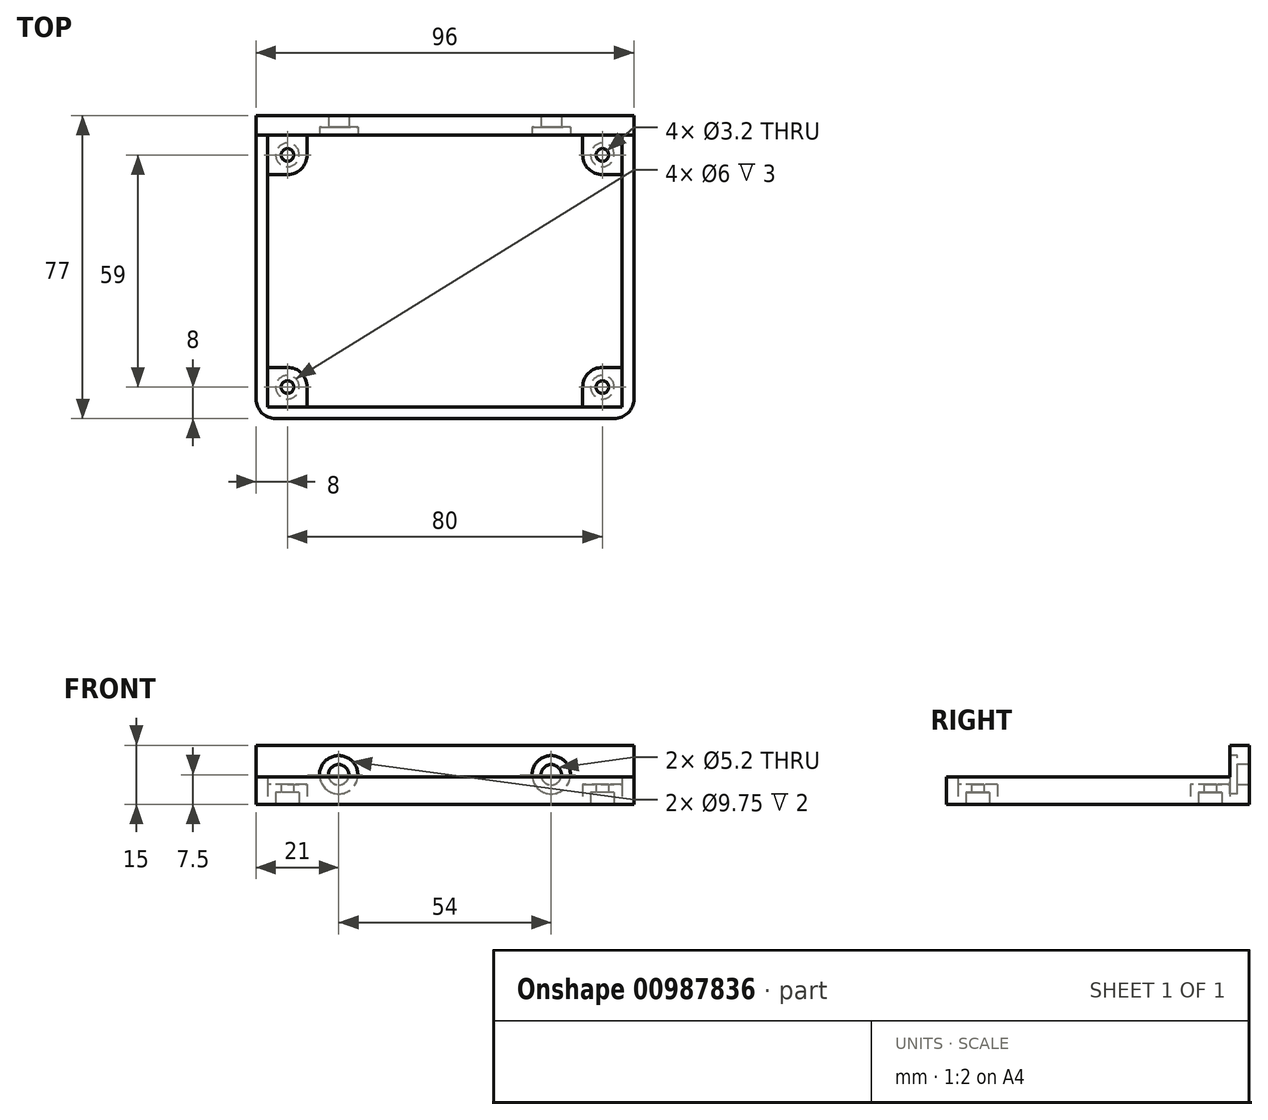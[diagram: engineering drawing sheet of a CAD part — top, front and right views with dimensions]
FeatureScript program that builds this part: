
annotation { "Feature Type Name" : "Feature", "Feature Type Description" : "" }
export const myFeature = defineFeature(function(context is Context, id is Id, definition is map)
    precondition{}
    {
        {
            var Q0;
            Q0=qCreatedBy(makeId("Top.planeOp"),FACE);
            var sketch = newSketch(context, id + "F0", { "sketchPlane" : qUnion([Q0])});
            skLineSegment(sketch, "E0.bottom", {"start": v(-40, 29.5) * mm, "end": v(40, 29.5) * mm, "construction": true});
            skLineSegment(sketch, "E0.top", {"start": v(-40, -29.5) * mm, "end": v(40, -29.5) * mm, "construction": true});
            skLineSegment(sketch, "E0.left", {"start": v(-40, 29.5) * mm, "end": v(-40, -29.5) * mm, "construction": true});
            skLineSegment(sketch, "E0.right", {"start": v(40, 29.5) * mm, "end": v(40, -29.5) * mm, "construction": true});
            skPoint(sketch, "E0.middle", {"position": v(0, 0) * mm});
            skLineSegment(sketch, "E1.bottom", {"start": v(-45, 34.5) * mm, "end": v(45, 34.5) * mm});
            skLineSegment(sketch, "E1.top", {"start": v(-45, -34.5) * mm, "end": v(45, -34.5) * mm});
            skLineSegment(sketch, "E1.left", {"start": v(-45, 34.5) * mm, "end": v(-45, -34.5) * mm});
            skLineSegment(sketch, "E1.right", {"start": v(45, 34.5) * mm, "end": v(45, -34.5) * mm});
            skCircle(sketch, "E2", {"center": v(-40, 29.5) * mm, "radius": 1.6 * mm});
            skCircle(sketch, "E3", {"center": v(-40, -29.5) * mm, "radius": 1.6 * mm});
            skCircle(sketch, "E4", {"center": v(40, -29.5) * mm, "radius": 1.6 * mm});
            skCircle(sketch, "E5", {"center": v(40, 29.5) * mm, "radius": 1.6 * mm});
            skCircle(sketch, "E6", {"center": v(-40, -29.5) * mm, "radius": 5 * mm});
            skLineSegment(sketch, "E7", {"start": v(-35, -29.5) * mm, "end": v(-35, -34.5) * mm});
            skLineSegment(sketch, "E8", {"start": v(-40, -24.5) * mm, "end": v(-45, -24.5) * mm});
            skCircle(sketch, "E9", {"center": v(-40, 29.5) * mm, "radius": 5 * mm});
            skCircle(sketch, "E10", {"center": v(40, 29.5) * mm, "radius": 5 * mm});
            skLineSegment(sketch, "E11", {"start": v(40, 24.5) * mm, "end": v(45, 24.5) * mm});
            skCircle(sketch, "E12", {"center": v(40, -29.5) * mm, "radius": 5 * mm});
            skLineSegment(sketch, "E13", {"start": v(35, -29.5) * mm, "end": v(35, -34.5) * mm});
            skLineSegment(sketch, "E14", {"start": v(40, -24.5) * mm, "end": v(45, -24.5) * mm});
            skLineSegment(sketch, "E15", {"start": v(35, 29.5) * mm, "end": v(35, 34.5) * mm});
            skLineSegment(sketch, "E16.bottom", {"start": v(-48, 39.5) * mm, "end": v(48, 39.5) * mm});
            skLineSegment(sketch, "E16.top", {"start": v(-48, -37.5) * mm, "end": v(48, -37.5) * mm});
            skLineSegment(sketch, "E16.left", {"start": v(-48, 39.5) * mm, "end": v(-48, -37.5) * mm});
            skLineSegment(sketch, "E16.right", {"start": v(48, 39.5) * mm, "end": v(48, -37.5) * mm});
            skLineSegment(sketch, "E17", {"start": v(-35, 29.5) * mm, "end": v(-35, 34.5) * mm});
            skLineSegment(sketch, "E18", {"start": v(-40, 24.5) * mm, "end": v(-45, 24.5) * mm});
            skCircle(sketch, "E19", {"center": v(40, 29.5) * mm, "radius": 3 * mm});
            skCircle(sketch, "E20", {"center": v(-40, 29.5) * mm, "radius": 3 * mm});
            skCircle(sketch, "E21", {"center": v(-40, -29.5) * mm, "radius": 3 * mm});
            skCircle(sketch, "E22", {"center": v(40, -29.5) * mm, "radius": 3 * mm});
            skLineSegment(sketch, "E23.top", {"start": v(-48, 34.5) * mm, "end": v(48, 34.5) * mm});
            skLineSegment(sketch, "E23.left", {"start": v(-48, 39.5) * mm, "end": v(-48, 34.5) * mm});
            skLineSegment(sketch, "E23.right", {"start": v(48, 39.5) * mm, "end": v(48, 34.5) * mm});
            skSolve(sketch);
        }
        {
            var Q0;
            Q0=makeQuery(id+"F0.imprint","IMPRINT",FACE,{"disambiguationData":[TD([[makeQuery(id+"F0.imprint","IMPRINT",EDGE,{"derivedFrom":sQuery(id+"F0.wireOp",EDGE,"E16.bottom")}),-1.0]])]});
            var Q1;
            {var subQ0=sQuery(id+"F0.wireOp",EDGE,"E7");Q1=makeQuery(id+"F0.imprint","IMPRINT",FACE,{"disambiguationData":[TD([[makeQuery(id+"F0.imprint","IMPRINT",EDGE,{"derivedFrom":subQ0}),-1.0]])]});}
            var Q2;
            {var subQ0=sQuery(id+"F0.wireOp",EDGE,"E1.left");var subQ1=sQuery(id+"F0.wireOp",EDGE,"E1.top");var subQ2=makeQuery(id+"F0.imprint","INTERSECT",VERTEX,{"derivedFrom":[subQ1,subQ0]});Q2=makeQuery(id+"F0.imprint","IMPRINT",FACE,{"disambiguationData":[TD([[makeQuery(id+"F0.imprint","IMPRINT",EDGE,{"disambiguationData":[TD([[subQ2,-1.0]])],"derivedFrom":subQ1}),1.0]])]});}
            var Q3;
            {var subQ0=sQuery(id+"F0.wireOp",EDGE,"E8");Q3=makeQuery(id+"F0.imprint","IMPRINT",FACE,{"disambiguationData":[TD([[makeQuery(id+"F0.imprint","IMPRINT",EDGE,{"derivedFrom":subQ0}),1.0]])]});}
            var Q4;
            Q4=makeQuery(id+"F0.imprint","IMPRINT",FACE,{"disambiguationData":[TD([[makeQuery(id+"F0.imprint","IMPRINT",EDGE,{"derivedFrom":sQuery(id+"F0.wireOp",EDGE,"E3")}),-1.0]])]});
            var Q5;
            {var subQ0=sQuery(id+"F0.wireOp",EDGE,"E13");Q5=makeQuery(id+"F0.imprint","IMPRINT",FACE,{"disambiguationData":[TD([[makeQuery(id+"F0.imprint","IMPRINT",EDGE,{"derivedFrom":subQ0}),1.0]])]});}
            var Q6;
            {var subQ0=sQuery(id+"F0.wireOp",EDGE,"E14");Q6=makeQuery(id+"F0.imprint","IMPRINT",FACE,{"disambiguationData":[TD([[makeQuery(id+"F0.imprint","IMPRINT",EDGE,{"derivedFrom":subQ0}),-1.0]])]});}
            var Q7;
            {var subQ0=sQuery(id+"F0.wireOp",EDGE,"E1.right");var subQ1=sQuery(id+"F0.wireOp",EDGE,"E1.top");var subQ2=makeQuery(id+"F0.imprint","INTERSECT",VERTEX,{"derivedFrom":[subQ1,subQ0]});Q7=makeQuery(id+"F0.imprint","IMPRINT",FACE,{"disambiguationData":[TD([[makeQuery(id+"F0.imprint","IMPRINT",EDGE,{"disambiguationData":[TD([[subQ2,1.0]])],"derivedFrom":subQ1}),1.0]])]});}
            var Q8;
            Q8=makeQuery(id+"F0.imprint","IMPRINT",FACE,{"disambiguationData":[TD([[makeQuery(id+"F0.imprint","IMPRINT",EDGE,{"derivedFrom":sQuery(id+"F0.wireOp",EDGE,"E4")}),-1.0]])]});
            var Q9;
            {var subQ0=sQuery(id+"F0.wireOp",EDGE,"E11");Q9=makeQuery(id+"F0.imprint","IMPRINT",FACE,{"disambiguationData":[TD([[makeQuery(id+"F0.imprint","IMPRINT",EDGE,{"derivedFrom":subQ0}),1.0]])]});}
            var Q10;
            {var subQ0=sQuery(id+"F0.wireOp",EDGE,"E1.right");var subQ1=sQuery(id+"F0.wireOp",EDGE,"E1.bottom");var subQ2=makeQuery(id+"F0.imprint","INTERSECT",VERTEX,{"derivedFrom":[subQ1,subQ0]});Q10=makeQuery(id+"F0.imprint","IMPRINT",FACE,{"disambiguationData":[TD([[makeQuery(id+"F0.imprint","IMPRINT",EDGE,{"disambiguationData":[TD([[subQ2,1.0]])],"derivedFrom":subQ1}),-1.0]])]});}
            var Q11;
            {var subQ0=sQuery(id+"F0.wireOp",EDGE,"E15");Q11=makeQuery(id+"F0.imprint","IMPRINT",FACE,{"disambiguationData":[TD([[makeQuery(id+"F0.imprint","IMPRINT",EDGE,{"derivedFrom":subQ0}),-1.0]])]});}
            var Q12;
            Q12=makeQuery(id+"F0.imprint","IMPRINT",FACE,{"disambiguationData":[TD([[makeQuery(id+"F0.imprint","IMPRINT",EDGE,{"derivedFrom":sQuery(id+"F0.wireOp",EDGE,"E5")}),-1.0]])]});
            var Q13;
            {var subQ0=sQuery(id+"F0.wireOp",EDGE,"E17");Q13=makeQuery(id+"F0.imprint","IMPRINT",FACE,{"disambiguationData":[TD([[makeQuery(id+"F0.imprint","IMPRINT",EDGE,{"derivedFrom":subQ0}),1.0]])]});}
            var Q14;
            {var subQ0=sQuery(id+"F0.wireOp",EDGE,"E1.left");var subQ1=sQuery(id+"F0.wireOp",EDGE,"E1.bottom");var subQ2=makeQuery(id+"F0.imprint","INTERSECT",VERTEX,{"derivedFrom":[subQ1,subQ0]});Q14=makeQuery(id+"F0.imprint","IMPRINT",FACE,{"disambiguationData":[TD([[makeQuery(id+"F0.imprint","IMPRINT",EDGE,{"disambiguationData":[TD([[subQ2,-1.0]])],"derivedFrom":subQ1}),-1.0]])]});}
            var Q15;
            {var subQ0=sQuery(id+"F0.wireOp",EDGE,"E18");Q15=makeQuery(id+"F0.imprint","IMPRINT",FACE,{"disambiguationData":[TD([[makeQuery(id+"F0.imprint","IMPRINT",EDGE,{"derivedFrom":subQ0}),-1.0]])]});}
            var Q16;
            Q16=makeQuery(id+"F0.imprint","IMPRINT",FACE,{"disambiguationData":[TD([[makeQuery(id+"F0.imprint","IMPRINT",EDGE,{"derivedFrom":sQuery(id+"F0.wireOp",EDGE,"E2")}),-1.0]])]});
            var Q17;
            Q17=makeQuery(id+"F0.imprint","IMPRINT",FACE,{"disambiguationData":[TD([[makeQuery(id+"F0.imprint","IMPRINT",EDGE,{"derivedFrom":sQuery(id+"F0.wireOp",EDGE,"E22")}),-1.0]])]});
            var Q18;
            Q18=makeQuery(id+"F0.imprint","IMPRINT",FACE,{"disambiguationData":[TD([[makeQuery(id+"F0.imprint","IMPRINT",EDGE,{"derivedFrom":sQuery(id+"F0.wireOp",EDGE,"E21")}),-1.0]])]});
            var Q19;
            Q19=makeQuery(id+"F0.imprint","IMPRINT",FACE,{"disambiguationData":[TD([[makeQuery(id+"F0.imprint","IMPRINT",EDGE,{"derivedFrom":sQuery(id+"F0.wireOp",EDGE,"E20")}),-1.0]])]});
            var Q20;
            Q20=makeQuery(id+"F0.imprint","IMPRINT",FACE,{"disambiguationData":[TD([[makeQuery(id+"F0.imprint","IMPRINT",EDGE,{"derivedFrom":sQuery(id+"F0.wireOp",EDGE,"E19")}),-1.0]])]});
            var Q21;
            {var subQ0=sQuery(id+"F0.wireOp",EDGE,"E23.top");var subQ1=sQuery(id+"F0.wireOp",EDGE,"E1.right");var subQ2=makeQuery(id+"F0.imprint","INTERSECT",VERTEX,{"derivedFrom":[subQ1,subQ0]});Q21=makeQuery(id+"F0.imprint","IMPRINT",FACE,{"disambiguationData":[TD([[makeQuery(id+"F0.imprint","IMPRINT",EDGE,{"disambiguationData":[TD([[subQ2,-1.0]])],"derivedFrom":subQ1}),-1.0]])]});}
            var Q22;
            {var subQ0=sQuery(id+"F0.wireOp",EDGE,"E23.top");var subQ1=sQuery(id+"F0.wireOp",EDGE,"E1.left");var subQ2=makeQuery(id+"F0.imprint","INTERSECT",VERTEX,{"derivedFrom":[subQ1,subQ0]});Q22=makeQuery(id+"F0.imprint","IMPRINT",FACE,{"disambiguationData":[TD([[makeQuery(id+"F0.imprint","IMPRINT",EDGE,{"disambiguationData":[TD([[subQ2,-1.0]])],"derivedFrom":subQ1}),1.0]])]});}
            extrude(context, id + "F1", {"entities" : qUnion([Q0, Q1, Q2, Q3, Q4, Q5, Q6, Q7, Q8, Q9, Q10, Q11, Q12, Q13, Q14, Q15, Q16, Q17, Q18, Q19, Q20, Q21, Q22]), "depth" : 5 * mm, "offsetDistance" : 25 * mm});
        }
        {
            var Q0;
            Q0 = qSketchRegion(id + "F0", true);
            var Q1;
            Q1=makeQuery(id+"F0.imprint","IMPRINT",FACE,{"disambiguationData":[TD([[makeQuery(id+"F0.imprint","IMPRINT",EDGE,{"derivedFrom":sQuery(id+"F0.wireOp",EDGE,"E16.bottom")}),-1.0]])]});
            extrude(context, id + "F2", {"entities" : qUnion([Q0, Q1]), "operationType" : NewBodyOperationType.ADD, "depth" : 7 * mm, "offsetDistance" : 25 * mm});
        }
        {
            var Q0;
            Q0=makeQuery(id+"F0.imprint","IMPRINT",FACE,{"disambiguationData":[TD([[makeQuery(id+"F0.imprint","IMPRINT",EDGE,{"derivedFrom":sQuery(id+"F0.wireOp",EDGE,"E3")}),-1.0]])]});
            var Q1;
            Q1=makeQuery(id+"F0.imprint","IMPRINT",FACE,{"disambiguationData":[TD([[makeQuery(id+"F0.imprint","IMPRINT",EDGE,{"derivedFrom":sQuery(id+"F0.wireOp",EDGE,"E4")}),-1.0]])]});
            var Q2;
            Q2=makeQuery(id+"F0.imprint","IMPRINT",FACE,{"disambiguationData":[TD([[makeQuery(id+"F0.imprint","IMPRINT",EDGE,{"derivedFrom":sQuery(id+"F0.wireOp",EDGE,"E5")}),-1.0]])]});
            var Q3;
            Q3=makeQuery(id+"F0.imprint","IMPRINT",FACE,{"disambiguationData":[TD([[makeQuery(id+"F0.imprint","IMPRINT",EDGE,{"derivedFrom":sQuery(id+"F0.wireOp",EDGE,"E2")}),-1.0]])]});
            var Q4;
            Q4=makeQuery(id+"F0.imprint","IMPRINT",FACE,{"disambiguationData":[TD([[makeQuery(id+"F0.imprint","IMPRINT",EDGE,{"derivedFrom":sQuery(id+"F0.wireOp",EDGE,"E5")}),-1.0]])]});
            var Q5;
            Q5=makeQuery(id+"F0.imprint","IMPRINT",FACE,{"disambiguationData":[TD([[makeQuery(id+"F0.imprint","IMPRINT",EDGE,{"derivedFrom":sQuery(id+"F0.wireOp",EDGE,"E4")}),-1.0]])]});
            var Q6;
            Q6=makeQuery(id+"F0.imprint","IMPRINT",FACE,{"disambiguationData":[TD([[makeQuery(id+"F0.imprint","IMPRINT",EDGE,{"derivedFrom":sQuery(id+"F0.wireOp",EDGE,"E3")}),-1.0]])]});
            var Q7;
            Q7=makeQuery(id+"F0.imprint","IMPRINT",FACE,{"disambiguationData":[TD([[makeQuery(id+"F0.imprint","IMPRINT",EDGE,{"derivedFrom":sQuery(id+"F0.wireOp",EDGE,"E2")}),-1.0]])]});
            extrude(context, id + "F3", {"entities" : qUnion([Q0, Q1, Q2, Q3, Q4, Q5, Q6, Q7]), "operationType" : NewBodyOperationType.REMOVE, "depth" : 3 * mm, "offsetDistance" : 25 * mm});
        }
        {
            var Q0;
            Q0=makeQuery(id+"F0.imprint","IMPRINT",FACE,{"disambiguationData":[TD([[makeQuery(id+"F0.imprint","IMPRINT",EDGE,{"derivedFrom":sQuery(id+"F0.wireOp",EDGE,"E16.bottom")}),-1.0]])]});
            extrude(context, id + "F4", {"entities" : qUnion([Q0]), "operationType" : NewBodyOperationType.ADD, "depth" : 15 * mm, "offsetDistance" : 25 * mm});
        }
        {
            var Q0;
            {var subQ0=sQuery(id+"F0.wireOp",EDGE,"E23.top");Q0=makeQuery(id+"F4.boolean.opBoolean","MERGE",FACE,{"derivedFrom":[makeQuery(id+"F2.opExtrude","SWEPT_FACE",FACE,{"disambiguationData":[OSD([subQ0])]}),makeQuery(id+"F4.opExtrude","SWEPT_FACE",FACE,{"disambiguationData":[OSD([subQ0])]})]});}
            var Q1;
            {var subQ0=sQuery(id+"F0.wireOp",EDGE,"E16.bottom");Q1=makeQuery(id+"F4.boolean.opBoolean","MERGE",FACE,{"derivedFrom":[makeQuery(id+"F2.opExtrude","SWEPT_FACE",FACE,{"disambiguationData":[OSD([subQ0])]}),makeQuery(id+"F4.opExtrude","SWEPT_FACE",FACE,{"disambiguationData":[OSD([subQ0])]})]});}
            var Q2;
            Q2=makeQuery(id+"F2.opExtrude","SWEPT_FACE",FACE,{"disambiguationData":[OSD([sQuery(id+"F0.wireOp",EDGE,"E16.top")])]});
            var Q3;
            {var subQ0=sQuery(id+"F0.wireOp",EDGE,"E23.top");Q3=makeQuery(id+"F4.boolean.opBoolean","MERGE",FACE,{"derivedFrom":[makeQuery(id+"F2.opExtrude","SWEPT_FACE",FACE,{"disambiguationData":[OSD([subQ0])]}),makeQuery(id+"F4.opExtrude","SWEPT_FACE",FACE,{"disambiguationData":[OSD([subQ0])]})]});}
            var sketch = newSketch(context, id + "F5", { "sketchPlane" : qUnion([Q0, Q1, Q2, Q3])});
            skCircle(sketch, "E24", {"center": v(-27, 7.5) * mm, "radius": 4.88 * mm});
            skCircle(sketch, "E25", {"center": v(27, 7.5) * mm, "radius": 4.88 * mm});
            skCircle(sketch, "E26", {"center": v(-27, 7.5) * mm, "radius": 2.6 * mm});
            skCircle(sketch, "E27", {"center": v(27, 7.5) * mm, "radius": 2.6 * mm});
            skSolve(sketch);
        }
        {
            var Q0;
            Q0=makeQuery(id+"F5.imprint","IMPRINT",FACE,{"disambiguationData":[TD([[makeQuery(id+"F5.imprint","IMPRINT",EDGE,{"derivedFrom":sQuery(id+"F5.wireOp",EDGE,"E27")}),1.0]])]});
            var Q1;
            Q1=makeQuery(id+"F5.imprint","IMPRINT",FACE,{"disambiguationData":[TD([[makeQuery(id+"F5.imprint","IMPRINT",EDGE,{"derivedFrom":sQuery(id+"F5.wireOp",EDGE,"E26")}),1.0]])]});
            extrude(context, id + "F6", {"entities" : qUnion([Q0, Q1]), "operationType" : NewBodyOperationType.REMOVE, "oppositeDirection" : true, "depth" : 25 * mm, "offsetDistance" : 25 * mm});
        }
        {
            var Q0;
            Q0=makeQuery(id+"F5.imprint","IMPRINT",FACE,{"disambiguationData":[TD([[makeQuery(id+"F5.imprint","IMPRINT",EDGE,{"derivedFrom":sQuery(id+"F5.wireOp",EDGE,"E24")}),1.0]])]});
            var Q1;
            Q1=makeQuery(id+"F5.imprint","IMPRINT",FACE,{"disambiguationData":[TD([[makeQuery(id+"F5.imprint","IMPRINT",EDGE,{"derivedFrom":sQuery(id+"F5.wireOp",EDGE,"E25")}),1.0]])]});
            extrude(context, id + "F7", {"entities" : qUnion([Q0, Q1]), "operationType" : NewBodyOperationType.REMOVE, "oppositeDirection" : true, "depth" : 2 * mm, "offsetDistance" : 25 * mm});
        }
        {
            var Q0;
            Q0=makeQuery(id+"F2.opExtrude","SWEPT_EDGE",EDGE,{"disambiguationData":[OSD([sQuery(id+"F0.wireOp",EDGE,"E16.top"),sQuery(id+"F0.wireOp",EDGE,"E16.left")])]});
            var Q1;
            Q1=makeQuery(id+"F2.opExtrude","SWEPT_EDGE",EDGE,{"disambiguationData":[OSD([sQuery(id+"F0.wireOp",EDGE,"E16.top"),sQuery(id+"F0.wireOp",EDGE,"E16.right")])]});
            var Q2;
            Q2=makeQuery(id+"F4.opExtrude","CAP_EDGE",EDGE,{"disambiguationData":[OSD([sQuery(id+"F0.wireOp",EDGE,"E23.right")])],"isStart":false});
            var Q3;
            Q3=makeQuery(id+"F4.opExtrude","CAP_EDGE",EDGE,{"disambiguationData":[OSD([sQuery(id+"F0.wireOp",EDGE,"E23.left")])],"isStart":false});
            fillet(context, id + "F8", {"entities" : qUnion([Q0, Q1, Q2, Q3]), "radius" : 5 * mm, "tangentPropagation" : true, "allowEdgeOverflow" : false});
        }
    });
